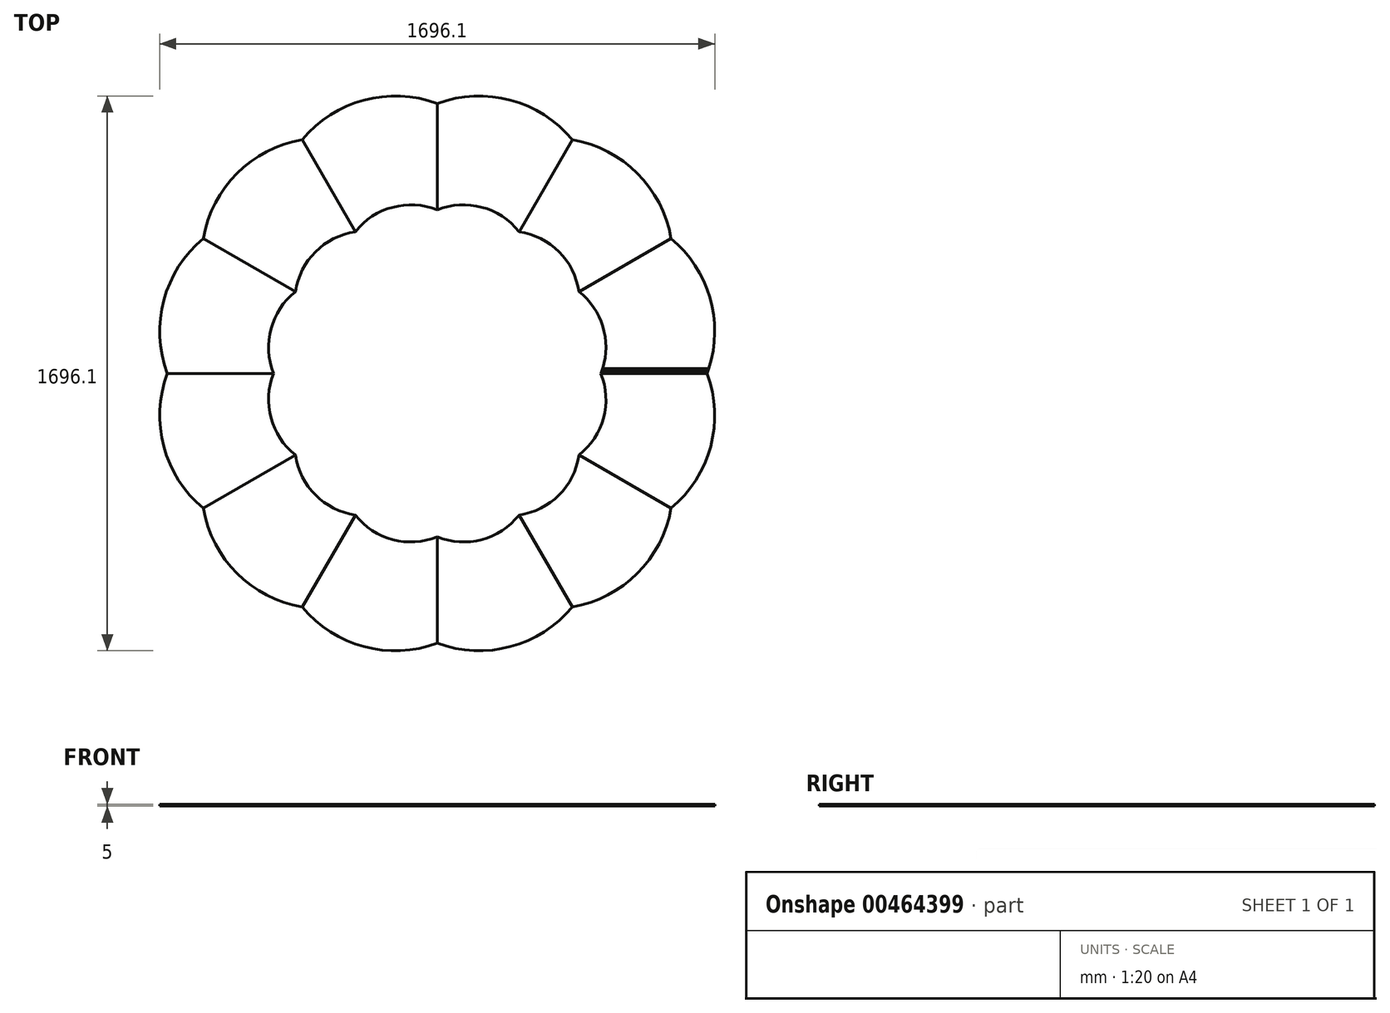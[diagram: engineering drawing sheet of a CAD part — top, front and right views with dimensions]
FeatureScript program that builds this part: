
annotation { "Feature Type Name" : "Feature", "Feature Type Description" : "" }
export const myFeature = defineFeature(function(context is Context, id is Id, definition is map)
    precondition{}
    {
        {
            var Q0;
            Q0=qCreatedBy(makeId("Top.planeOp"),FACE);
            var sketch = newSketch(context, id + "F0", { "sketchPlane" : qUnion([Q0])});
            skLineSegment(sketch, "E0", {"start": v(-904.12, 0) * mm, "end": v(1128.65, 0) * mm, "construction": true});
            skLineSegment(sketch, "E1", {"start": v(0, -926.5) * mm, "end": v(0, 989.29) * mm, "construction": true});
            skLineSegment(sketch, "E2", {"start": v(0, 0) * mm, "end": v(1007.14, 581.47) * mm, "construction": true});
            skCircle(sketch, "E3", {"center": v(0, 0) * mm, "radius": 900 * mm});
            skCircle(sketch, "E4", {"center": v(0, 0) * mm, "radius": 400 * mm, "construction": true});
            skCircle(sketch, "E5", {"center": v(0, 0) * mm, "radius": 600 * mm, "construction": true});
            skCircle(sketch, "E6", {"center": v(0, 0) * mm, "radius": 825 * mm, "construction": true});
            skLineSegment(sketch, "E7", {"start": v(0, 0) * mm, "end": v(1160.83, 311.04) * mm, "construction": true});
            skArc(sketch, "E8", {"start": v(825, 0) * mm, "mid": v(868.98, 232.84) * mm, "end": v(714.47, 412.5) * mm});
            skCircle(sketch, "E9", {"center": v(0, 0) * mm, "radius": 500 * mm, "construction": true});
            skArc(sketch, "E10", {"start": v(500, 0) * mm, "mid": v(508.08, 136.14) * mm, "end": v(433.01, 250) * mm});
            skArc(sketch, "E11", {"start": v(825, 0) * mm, "mid": v(835.48, 223.86) * mm, "end": v(714.47, 412.5) * mm});
            skLineSegment(sketch, "E12", {"start": v(433.01, 250) * mm, "end": v(714.47, 412.5) * mm});
            skLineSegment(sketch, "E13", {"start": v(500, 0) * mm, "end": v(523.18, 0) * mm});
            skLineSegment(sketch, "E14", {"start": v(825, 0) * mm, "end": v(500, 0) * mm});
            skSolve(sketch);
        }
        {
            var Q0;
            {var subQ3=sQuery(id+"F0.wireOp",EDGE,"E10");Q0=makeQuery(id+"F0.imprint","IMPRINT",FACE,{"disambiguationData":[TD([[makeQuery(id+"F0.imprint","IMPRINT",EDGE,{"derivedFrom":subQ3}),-1.0]])]});}
            extrude(context, id + "F1", {"entities" : qUnion([Q0]), "depth" : 5 * mm});
        }
        {
            var Q0;
            Q0=qCreatedBy(makeId("Right.planeOp"),FACE);
            var sketch = newSketch(context, id + "F2", { "sketchPlane" : qUnion([Q0])});
            skLineSegment(sketch, "E15", {"start": v(0, 65.35) * mm, "end": v(0, -84.37) * mm, "construction": true});
            skSolve(sketch);
        }
        {
            var Q0;
            Q0=makeQuery(id+"F1.opExtrude","SWEPT_BODY",BODY,{"disambiguationData":[OSD([sQuery(id+"F0.wireOp",EDGE,"E10"),sQuery(id+"F0.wireOp",EDGE,"E11"),sQuery(id+"F0.wireOp",EDGE,"E12"),sQuery(id+"F0.wireOp",EDGE,"E14")])]});
            var Q1;
            Q1=sQuery(id+"F2.wireOp",EDGE,"E15");
            circularPattern(context, id + "F3", {"entities" : qUnion([Q0]), "axis" : qUnion([Q1]), "angle" : 360 * degree, "instanceCount" : 12, "equalSpace" : true});
        }
        {
            var Q0;
            Q0=makeQuery(id+"F1.opExtrude","CAP_FACE",FACE,{"disambiguationData":[OSD([sQuery(id+"F0.wireOp",EDGE,"E10"),sQuery(id+"F0.wireOp",EDGE,"E11"),sQuery(id+"F0.wireOp",EDGE,"E12"),sQuery(id+"F0.wireOp",EDGE,"E14")])],"isStart":false});
            var sketch = newSketch(context, id + "F4", { "sketchPlane" : qUnion([Q0])});
            skLineSegment(sketch, "E16", {"start": v(502.4, 6.27) * mm, "end": v(827.26, 6.27) * mm});
            skLineSegment(sketch, "E17", {"start": v(505.27, 14.72) * mm, "end": v(830.1, 14.72) * mm});
            skSolve(sketch);
        }
        {
            var Q0;
            {var subQ0=sQuery(id+"F4.wireOp",EDGE,"E16");Q0=makeQuery(id+"F4.imprint","IMPRINT",FACE,{"disambiguationData":[TD([[makeQuery(id+"F4.imprint","IMPRINT",EDGE,{"derivedFrom":subQ0}),1.0]])]});}
            extrude(context, id + "F5", {"entities" : qUnion([Q0]), "operationType" : NewBodyOperationType.REMOVE, "oppositeDirection" : true, "depth" : 2 * mm, "hasDraft" : true, "draftAngle" : 45 * degree, "draftPullDirection" : true});
        }
    });
